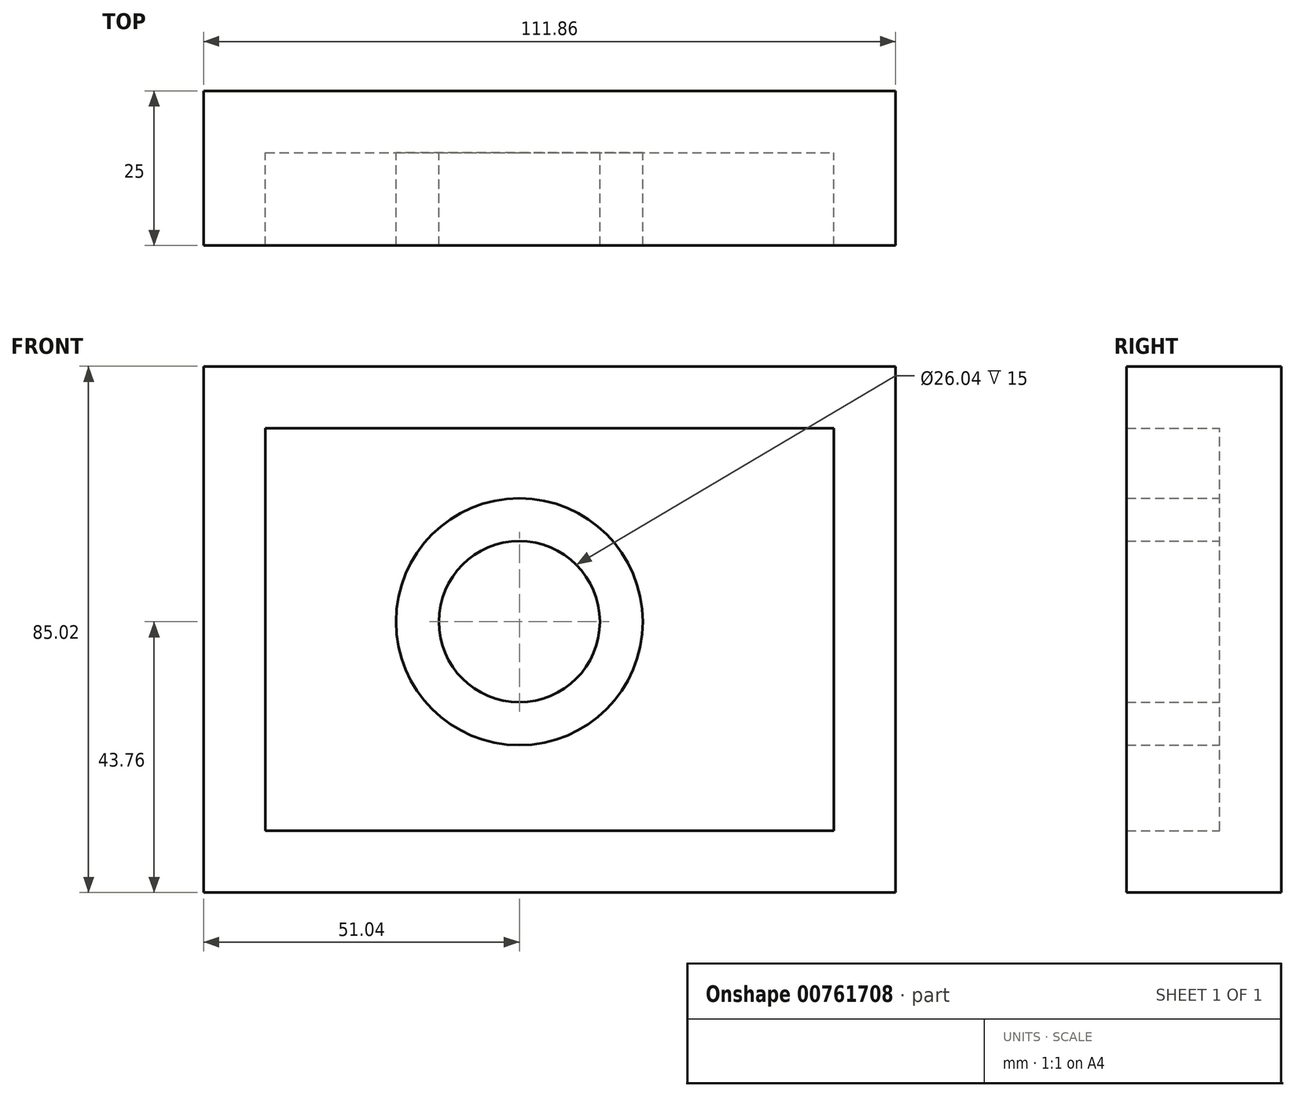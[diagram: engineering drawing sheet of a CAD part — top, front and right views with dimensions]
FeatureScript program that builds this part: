
annotation { "Feature Type Name" : "Feature", "Feature Type Description" : "" }
export const myFeature = defineFeature(function(context is Context, id is Id, definition is map)
    precondition{}
    {
        {
            var Q0;
            Q0=qCreatedBy(makeId("Front.planeOp"),FACE);
            var sketch = newSketch(context, id + "F0", { "sketchPlane" : qUnion([Q0])});
            skLineSegment(sketch, "E0.bottom", {"start": v(-51.04, -43.76) * mm, "end": v(60.82, -43.76) * mm});
            skLineSegment(sketch, "E0.top", {"start": v(-51.04, 41.26) * mm, "end": v(60.82, 41.26) * mm});
            skLineSegment(sketch, "E0.left", {"start": v(-51.04, -43.76) * mm, "end": v(-51.04, 41.26) * mm});
            skLineSegment(sketch, "E0.right", {"start": v(60.82, -43.76) * mm, "end": v(60.82, 41.26) * mm});
            skSolve(sketch);
        }
        {
            var Q0;
            Q0=makeQuery(id+"F0.imprint","IMPRINT",FACE,{"disambiguationData":[TD([[makeQuery(id+"F0.imprint","IMPRINT",EDGE,{"derivedFrom":sQuery(id+"F0.wireOp",EDGE,"E0.bottom")}),1.0]])]});
            extrude(context, id + "F1", {"entities" : qUnion([Q0]), "depth" : 25 * mm, "offsetDistance" : 25 * mm});
        }
        {
            var Q0;
            Q0=makeQuery(id+"F1.opExtrude","CAP_FACE",FACE,{"disambiguationData":[OSD([sQuery(id+"F0.wireOp",EDGE,"E0.bottom"),sQuery(id+"F0.wireOp",EDGE,"E0.top"),sQuery(id+"F0.wireOp",EDGE,"E0.left"),sQuery(id+"F0.wireOp",EDGE,"E0.right")])],"isStart":false});
            shell(context, id + "F2", {"entities" : qUnion([Q0]), "thickness" : 10 * mm});
        }
        {
            var Q0;
            Q0=qCreatedBy(makeId("Front.planeOp"),FACE);
            var sketch = newSketch(context, id + "F3", { "sketchPlane" : qUnion([Q0])});
            skCircle(sketch, "E1", {"center": v(0, 0) * mm, "radius": 19.94 * mm});
            skLineSegment(sketch, "E2", {"start": v(-6.74, -18.76) * mm, "end": v(-6.74, -33.98) * mm});
            skLineSegment(sketch, "E3.MirrorCS", {"start": v(6.74, -18.76) * mm, "end": v(6.74, -33.98) * mm});
            skCircle(sketch, "E4", {"center": v(0, 0) * mm, "radius": 13.02 * mm});
            skSolve(sketch);
        }
        {
            var Q0;
            Q0 = qSketchRegion(id + "F3", true);
            extrude(context, id + "F4", {"entities" : qUnion([Q0]), "operationType" : NewBodyOperationType.ADD, "depth" : 25 * mm, "offsetDistance" : 25 * mm});
        }
    });
